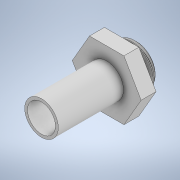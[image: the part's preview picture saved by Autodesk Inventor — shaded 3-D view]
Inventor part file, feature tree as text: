
AUTODESK INVENTOR PART (.ipt)
format: ipt  version: 2021 (Build 250183000, 183)  size: 230,400 bytes
history: native  units: mm
features: sketch x7, extrude x5, helix x1, revolve x1, projected_geometry x1
ambient origin geometry x8: Origin, YZ Plane, XZ Plane, XY Plane, X Axis, Y Axis, Z Axis, Center Point
bodies: Solid1 (feature_tree)
feature tree (15):
  extrude  "Extrusion1"  Depth=8.0mm TaperAngle=0.0deg
  extrude  "Extrusion2"  Depth=8.0mm TaperAngle=0.0deg
  helix  "Coil1"  [1 undecoded]
  extrude  "Extrusion3"  Depth=23.5mm
  revolve  "Revolution1"  Angle=60.0deg
  extrude  "Extrusion4"  Depth=8.0mm TaperAngle=0.0deg
  extrude  "Extrusion5"  Depth=10.0mm
  sketch  "Sketch1"  dims[d0=32.0mm d1=8.0mm d2=0.0mm]
  sketch  "Sketch2"  dims[d3=19.85mm d4=8.0mm d5=0.0mm d6=19.85mm]
  sketch  "Sketch3"  dims[d7=21.8mm d8=23.5mm]
  sketch  "Sketch4"  dims[d9=30.0deg d10=60.0deg]
  sketch  "Sketch5"  dims[d11=1.5mm]
  sketch  "Sketch6"  dims[d12=3.0mm d13=15.0mm d14=10.0mm d15=0.0mm d16=90.0deg d17=90.0deg d18=0.0mm d19=0.0mm d20=8.0mm d21=0.0mm]
  sketch  "Sketch7"  dims[d22=10.0mm d23=11.8mm d24=45.0deg d25=90.0deg d26=18.0mm d27=35.0mm d28=0.0mm d29=1.5mm d30=0.0mm d31=0.0mm]
  projected_geometry  "Projected Loop1"
note: 1 required parameter value undecoded (feature->parameter linkage not recoverable at this tier; creation-order binding heuristic only, values carry confidence <= 0.55)
